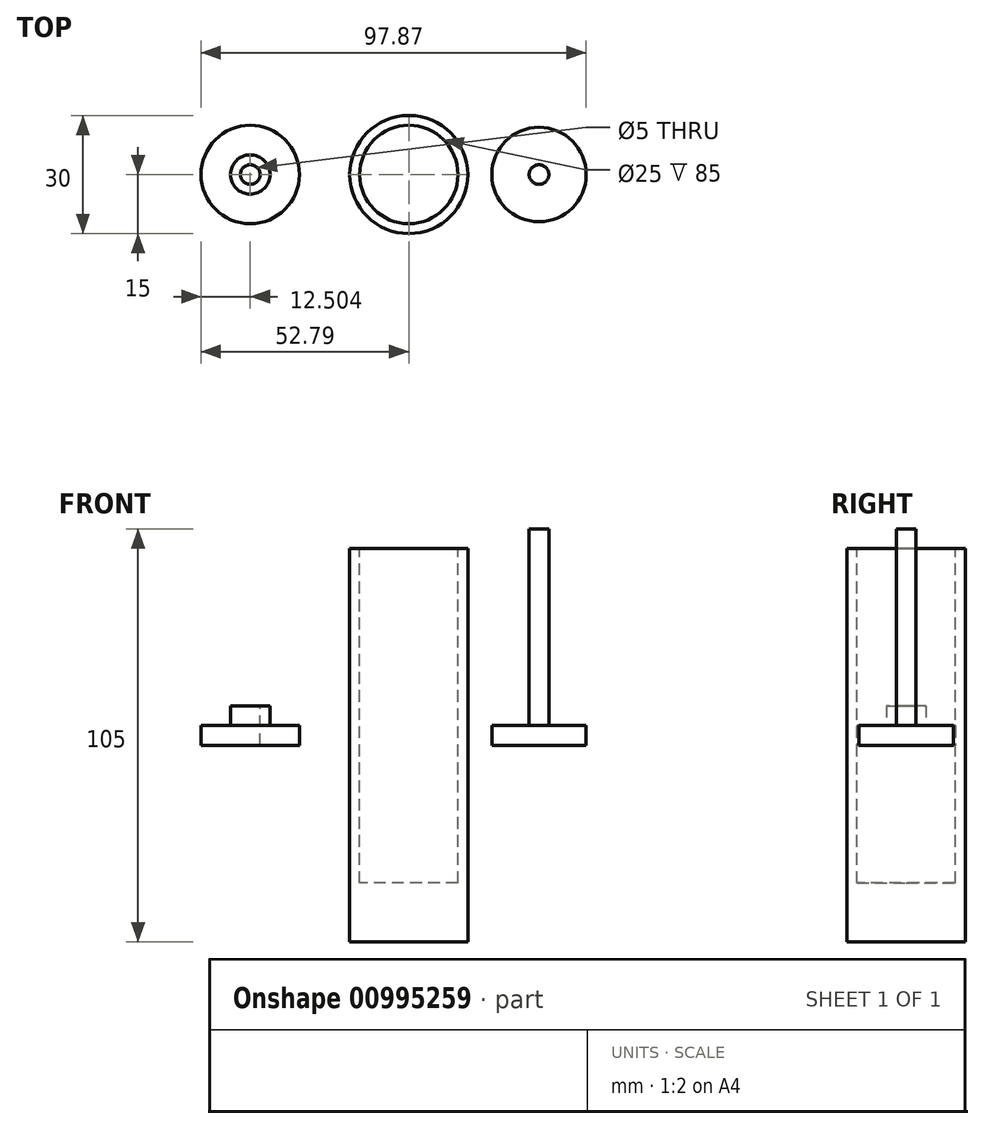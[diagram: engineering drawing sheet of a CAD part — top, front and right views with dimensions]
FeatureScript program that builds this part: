
annotation { "Feature Type Name" : "Feature", "Feature Type Description" : "" }
export const myFeature = defineFeature(function(context is Context, id is Id, definition is map)
    precondition{}
    {
        {
            var Q0;
            Q0=qCreatedBy(makeId("Top.planeOp"),FACE);
            var sketch = newSketch(context, id + "F0", { "sketchPlane" : qUnion([Q0])});
            skCircle(sketch, "E0", {"center": v(0, 0) * mm, "radius": 15 * mm});
            skSolve(sketch);
        }
        {
            var Q0;
            Q0 = qSketchRegion(id + "F0", true);
            extrude(context, id + "F1", {"entities" : qUnion([Q0]), "endBound" : BoundingType.SYMMETRIC, "depth" : 100 * mm, "offsetDistance" : 25 * mm});
        }
        {
            var Q0;
            Q0=makeQuery(id+"F1.opExtrude","CAP_FACE",FACE,{"disambiguationData":[OSD([sQuery(id+"F0.wireOp",EDGE,"E0")])],"isStart":false});
            var sketch = newSketch(context, id + "F2", { "sketchPlane" : qUnion([Q0])});
            skCircle(sketch, "E1", {"center": v(0, 0) * mm, "radius": 12.5 * mm});
            skSolve(sketch);
        }
        {
            var Q0;
            Q0=makeQuery(id+"F2.imprint","IMPRINT",FACE,{"disambiguationData":[TD([[makeQuery(id+"F2.imprint","IMPRINT",EDGE,{"derivedFrom":sQuery(id+"F2.wireOp",EDGE,"E1")}),1.0]])]});
            extrude(context, id + "F3", {"entities" : qUnion([Q0]), "operationType" : NewBodyOperationType.REMOVE, "oppositeDirection" : true, "depth" : 85 * mm, "offsetDistance" : 25 * mm});
        }
        {
            var Q0;
            Q0=qCreatedBy(makeId("Top.planeOp"),FACE);
            var sketch = newSketch(context, id + "F4", { "sketchPlane" : qUnion([Q0])});
            skCircle(sketch, "E2", {"center": v(33.08, 0) * mm, "radius": 12 * mm});
            skSolve(sketch);
        }
        {
            var Q0;
            Q0 = qSketchRegion(id + "F4", true);
            extrude(context, id + "F5", {"entities" : qUnion([Q0]), "depth" : 5 * mm, "offsetDistance" : 25 * mm});
        }
        {
            var Q0;
            Q0=makeQuery(id+"F5.opExtrude","CAP_FACE",FACE,{"disambiguationData":[OSD([sQuery(id+"F4.wireOp",EDGE,"E2")])],"isStart":false});
            var sketch = newSketch(context, id + "F6", { "sketchPlane" : qUnion([Q0])});
            skCircle(sketch, "E3", {"center": v(33.08, 0) * mm, "radius": 2.5 * mm});
            skSolve(sketch);
        }
        {
            var Q0;
            Q0 = qSketchRegion(id + "F6", true);
            extrude(context, id + "F7", {"entities" : qUnion([Q0]), "operationType" : NewBodyOperationType.ADD, "depth" : 50 * mm, "offsetDistance" : 25 * mm});
        }
        {
            var Q0;
            Q0=qCreatedBy(makeId("Top.planeOp"),FACE);
            var sketch = newSketch(context, id + "F8", { "sketchPlane" : qUnion([Q0])});
            skCircle(sketch, "E4", {"center": v(-40.29, 0) * mm, "radius": 12.5 * mm});
            skSolve(sketch);
        }
        {
            var Q0;
            Q0 = qSketchRegion(id + "F8", true);
            extrude(context, id + "F9", {"entities" : qUnion([Q0]), "depth" : 5 * mm, "offsetDistance" : 25 * mm});
        }
        {
            var Q0;
            Q0=makeQuery(id+"F9.opExtrude","CAP_FACE",FACE,{"disambiguationData":[OSD([sQuery(id+"F8.wireOp",EDGE,"E4")])],"isStart":false});
            var sketch = newSketch(context, id + "F10", { "sketchPlane" : qUnion([Q0])});
            skCircle(sketch, "E5", {"center": v(-40.29, 0) * mm, "radius": 5 * mm});
            skSolve(sketch);
        }
        {
            var Q0;
            Q0 = qSketchRegion(id + "F10", true);
            extrude(context, id + "F11", {"entities" : qUnion([Q0]), "operationType" : NewBodyOperationType.ADD, "depth" : 5 * mm, "offsetDistance" : 25 * mm});
        }
        {
            var Q0;
            Q0=makeQuery(id+"F11.opExtrude","CAP_FACE",FACE,{"disambiguationData":[OSD([sQuery(id+"F10.wireOp",EDGE,"E5")])],"isStart":false});
            var sketch = newSketch(context, id + "F12", { "sketchPlane" : qUnion([Q0])});
            skCircle(sketch, "E6", {"center": v(-40.29, 0) * mm, "radius": 2.5 * mm});
            skSolve(sketch);
        }
        {
            var Q0;
            Q0 = qSketchRegion(id + "F12", true);
            extrude(context, id + "F13", {"entities" : qUnion([Q0]), "operationType" : NewBodyOperationType.REMOVE, "oppositeDirection" : true, "depth" : 10 * mm, "offsetDistance" : 25 * mm});
        }
    });
